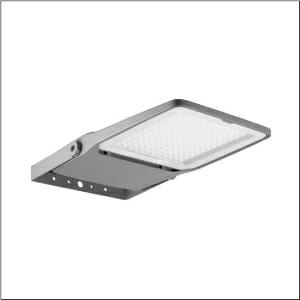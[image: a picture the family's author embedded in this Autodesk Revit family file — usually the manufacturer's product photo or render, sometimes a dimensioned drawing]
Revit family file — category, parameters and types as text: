
# Revit family: floodlight_fl_20_midi___rs17_5xa7682d3b2ac_ca3f
name_source: partatom
category: Lighting Fixtures
units: mm (PartAtom-declared; Revit-internal decimal feet)

## family parameters
Cut with Voids When Loaded = No
Host = Face
Light Source = No
Part Type = Normal
Room Calculation Point = No
Round Connector Dimension = Use Diameter
Shared = No

## types (1)
- --- (1 x LED 5000K / CRI = 70 (unbekannt), 19830 lm, 5000K)
    Apparent Load = 142 VA
    CIE Flux Codes = 79 92 99 100 100
    Color Rendering = 70
    Color Temperature = 5000K
    Default Elevation = 1800 mm
    Description = Floodlight FL 20 midi, floodlight, primary light control with lens, of plastic, primary optical cover: protective disc, of toughened safety glass, transparent, light distribution: RS17, light emission: direct distribution, primary light characteristic: rotationally symmetric, installation type: surface-mounted, LED, High Power LED, rated luminous flux: 19.830lm, luminous efficacy: 140lm/W, light colour: 750, colour temperature: 5000K, control gear: ECG Plus, control: flexible luminous flux parameterisation, time-dependent luminous flux control, digital communication interface, power reduction, overheat protection, electronic power reduction, with terminal, 5-pole, max. 2.5mm², mains connection: 220..240V, AC, 50/60Hz, rated input power: 142W, LED unit, of diecast aluminium, powder-coated, Siteco® metallic grey (DB 702S), corrosivity category C5 mid according to DIN EN ISO 12944, incl. 1x M20 cable gland for cable Ø 6.5..12mm, length: 731mm, width: 450mm, height: 76mm, housing frame, of diecast aluminium, powder-coated, Siteco® metallic grey (DB 702S), wall fastening, of steel, powder-coated, Siteco® metallic grey (DB 702S), DALI, protection rating (complete): IP66, insulation class (complete): insulation class II (safety insulation), certification: CE, ENEC, VDE, protection symbol: D, permissible operating ambient temperature: -40..+40°C, permissible operating ambient temperature for outdoor applications: -40..+50°C, standard: DIN EN 12944, packaging unit: 1 piece

Light Distribution: RS17
    Height = 76 mm
    Lamp = 1 x LED 5000K / CRI >= 70 (unbekannt)
    Lamp Light Flux = 19830 lm
    Lamp count = 1
    Length = 731 mm
    Luminous efficacy = 140 lm/W
    Manufacturer = Siteco
    ModVariant = No
    Model = 5XA7682D3B2AC
    Mounting Place = Wall
    Mounting Type = Surface mounted
    Number of Poles = 1
    OnlyDefault = Yes
    Power Factor = 1
    Product Name = Floodlight FL 20 midi | RS17
    Product group = floodlight | wall mounted
    ProductGroupID = 2001
    Protection Class = Protection class II
    Protection Degree = IP 66
    RLX_Detail_Level = 1
    RLX_Emergency_Light_Flux = 0 lm
    RLX_Emergency_Type = 0
    RLX_Emergency_Type_DB = No
    RlxData = <blob elided: 86881 chars, md5=fa34cbf5>
    Socket = socket
    Standby Power = 0 W
    System Light Flux = 19830 lm
    System Power = 142 W
    Type Comments = factory setting: luminous flux: 100 % | dim-lin: 254 | 489 mA
    Type Image = l_1005944.jpg
    URL = http://relux.com
    VarID = @adj_146557
    Voltage = 0 V
    Weight = 0.00 kg
    Width = 450 mm

## geometry (parser evidence)
native form markers: Blend x4, Sweep x12
no freeform markers — native parametric forms only
